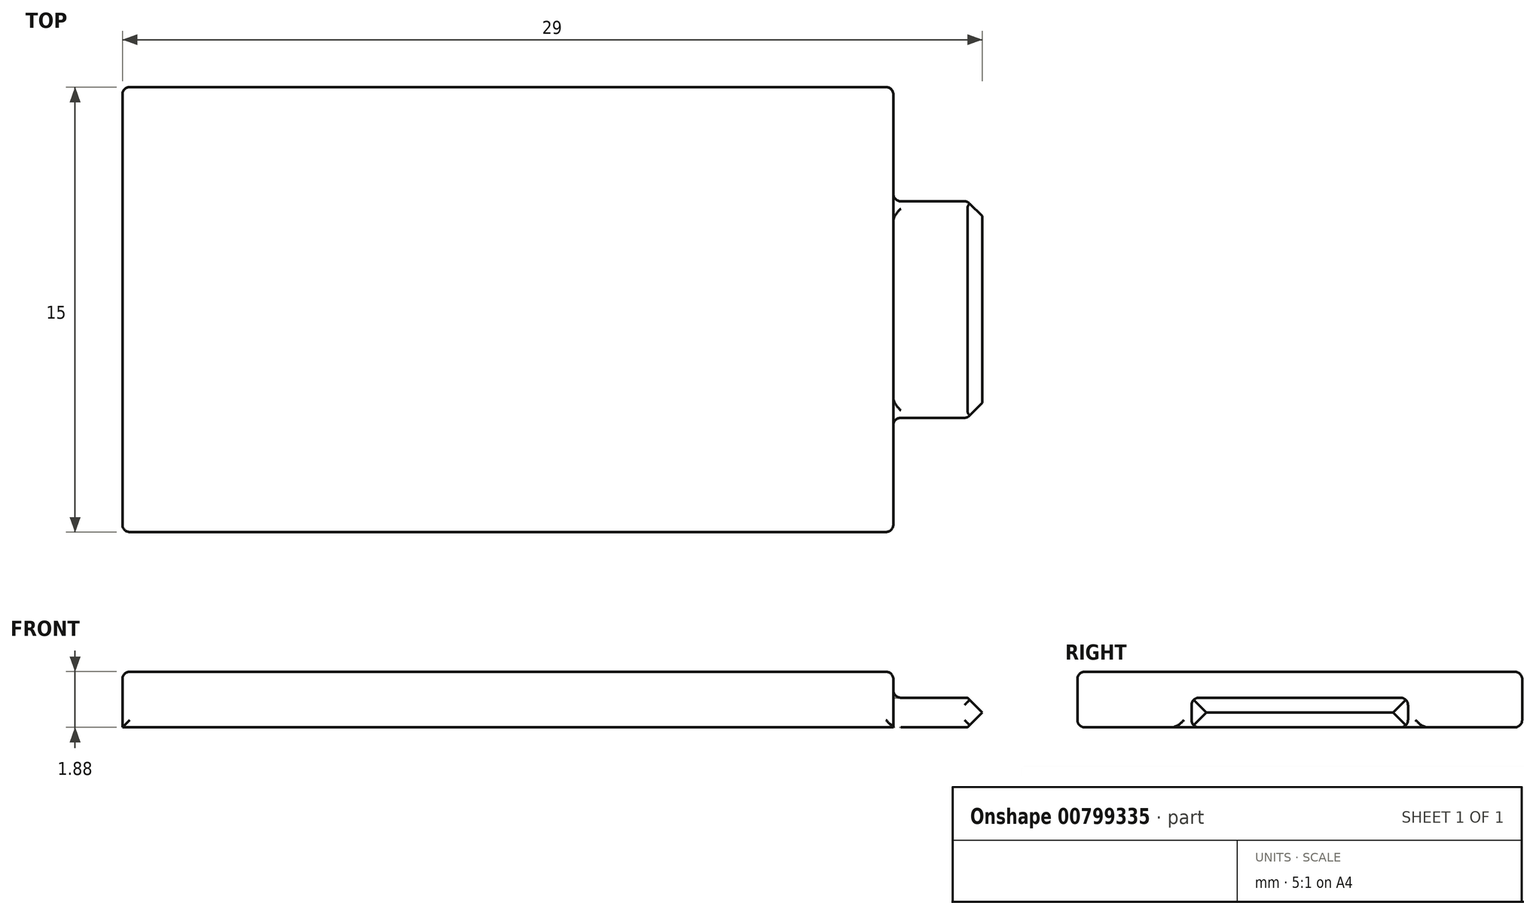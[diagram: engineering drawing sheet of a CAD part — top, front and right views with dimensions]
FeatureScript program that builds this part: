
annotation { "Feature Type Name" : "Feature", "Feature Type Description" : "" }
export const myFeature = defineFeature(function(context is Context, id is Id, definition is map)
    precondition{}
    {
        {
            var Q0;
            Q0=qCreatedBy(makeId("Top.planeOp"),FACE);
            var sketch = newSketch(context, id + "F0", { "sketchPlane" : qUnion([Q0])});
            skLineSegment(sketch, "E0.bottom", {"start": v(24.6, 2.54) * mm, "end": v(50.6, 2.54) * mm});
            skLineSegment(sketch, "E0.top", {"start": v(24.6, -12.46) * mm, "end": v(50.6, -12.46) * mm});
            skLineSegment(sketch, "E0.left", {"start": v(24.6, 2.54) * mm, "end": v(24.6, -12.46) * mm});
            skLineSegment(sketch, "E0.right", {"start": v(50.6, 2.54) * mm, "end": v(50.6, -12.46) * mm});
            skSolve(sketch);
        }
        {
            var Q0;
            Q0 = qSketchRegion(id + "F0", true);
            extrude(context, id + "F1", {"entities" : qUnion([Q0]), "depth" : 1.88 * mm, "offsetDistance" : 25 * mm});
        }
        {
            var Q0;
            Q0=makeQuery(id+"F1.opExtrude","SWEPT_FACE",FACE,{"disambiguationData":[OSD([sQuery(id+"F0.wireOp",EDGE,"E0.right")])]});
            var sketch = newSketch(context, id + "F2", { "sketchPlane" : qUnion([Q0])});
            skLineSegment(sketch, "E1.bottom", {"start": v(-8.6, 1) * mm, "end": v(-1.3, 1) * mm});
            skLineSegment(sketch, "E1.top", {"start": v(-8.6, 0) * mm, "end": v(-1.3, 0) * mm});
            skLineSegment(sketch, "E1.left", {"start": v(-8.6, 1) * mm, "end": v(-8.6, 0) * mm});
            skLineSegment(sketch, "E1.right", {"start": v(-1.3, 1) * mm, "end": v(-1.3, 0) * mm});
            skSolve(sketch);
        }
        {
            var Q0;
            Q0 = qSketchRegion(id + "F2", true);
            extrude(context, id + "F3", {"entities" : qUnion([Q0]), "operationType" : NewBodyOperationType.ADD, "depth" : 3 * mm, "offsetDistance" : 25 * mm});
        }
        {
            var Q0;
            Q0=makeQuery(id+"F3.opExtrude","CAP_FACE",FACE,{"disambiguationData":[OSD([sQuery(id+"F2.wireOp",EDGE,"E1.bottom"),sQuery(id+"F2.wireOp",EDGE,"E1.top"),sQuery(id+"F2.wireOp",EDGE,"E1.left"),sQuery(id+"F2.wireOp",EDGE,"E1.right")])],"isStart":false});
            chamfer(context, id + "F4", {"entities" : qUnion([Q0]), "width" : .5 * mm, "tangentPropagation" : true});
        }
        {
            var Q0;
            Q0=makeQuery(id+"F3.opExtrude","SWEPT_FACE",FACE,{"disambiguationData":[OSD([sQuery(id+"F2.wireOp",EDGE,"E1.left")])]});
            var Q1;
            Q1=makeQuery(id+"F3.opExtrude","SWEPT_FACE",FACE,{"disambiguationData":[OSD([sQuery(id+"F2.wireOp",EDGE,"E1.right")])]});
            var Q2;
            Q2=makeQuery(id+"F1.opExtrude","CAP_FACE",FACE,{"disambiguationData":[OSD([sQuery(id+"F0.wireOp",EDGE,"E0.bottom"),sQuery(id+"F0.wireOp",EDGE,"E0.top"),sQuery(id+"F0.wireOp",EDGE,"E0.left"),sQuery(id+"F0.wireOp",EDGE,"E0.right")])],"isStart":false});
            var Q3;
            Q3=makeQuery(id+"F1.opExtrude","SWEPT_FACE",FACE,{"disambiguationData":[OSD([sQuery(id+"F0.wireOp",EDGE,"E0.top")])]});
            var Q4;
            Q4=makeQuery(id+"F1.opExtrude","SWEPT_FACE",FACE,{"disambiguationData":[OSD([sQuery(id+"F0.wireOp",EDGE,"E0.bottom")])]});
            fillet(context, id + "F5", {"entities" : qUnion([Q0, Q1, Q2, Q3, Q4]), "radius" : .25 * mm, "tangentPropagation" : true, "allowEdgeOverflow" : false});
        }
    });
